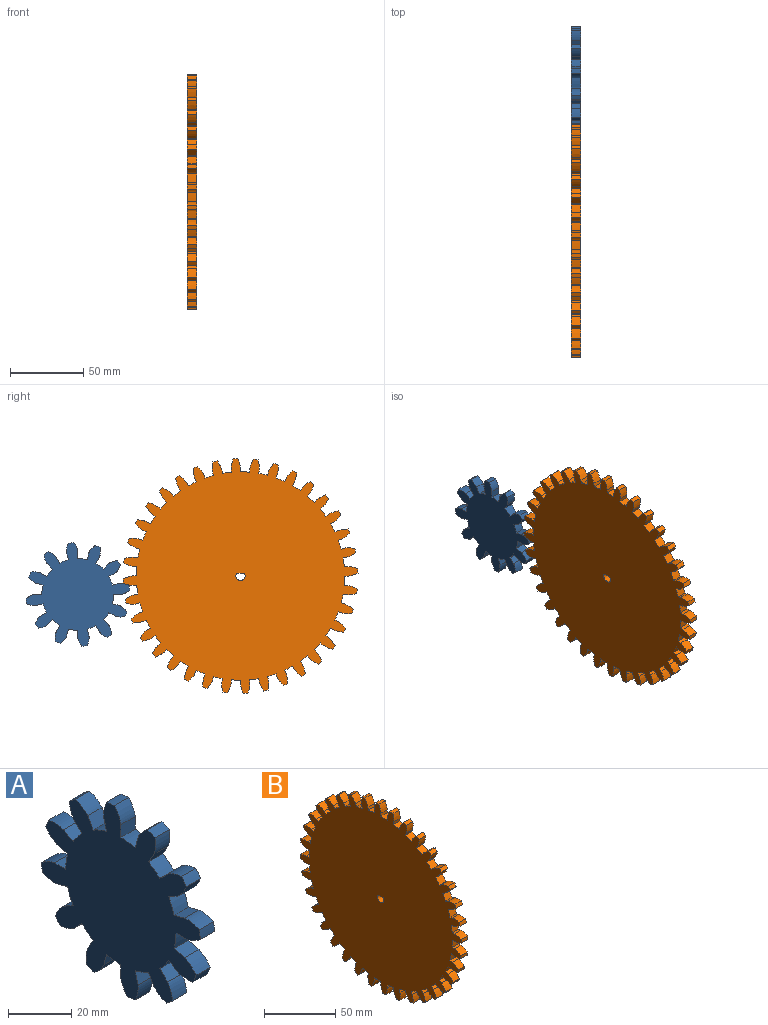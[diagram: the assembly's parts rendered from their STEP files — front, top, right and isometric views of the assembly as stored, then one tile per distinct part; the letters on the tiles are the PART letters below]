
ASSEMBLY  parts=2 mates=1
PART A: 74 faces, bbox 6.4x70.9x70.9 mm
  f0: cylinder r=24.6mm len=6.35mm, axis (-1,0,0), area 40.9mm2, adj f5,f7,f72,f73
  f1: plane 6.35x4.74mm, normal (0,-0.26,0.97), area 31.2mm2, adj f2,f66,f72,f73
  f2: extruded ~6.35x4.99mm, area 42.4mm2, adj f1,f3,f72,f73
  f3: cylinder r=35.56mm len=6.35mm, axis (-1,0,0), area 22.7mm2, adj f2,f4,f72,f73
  f4: extruded ~6.57x6.35mm, area 42.4mm2, adj f3,f5,f72,f73
  f5: plane 6.35x4.25mm, normal (0,0.5,-0.87), area 31.2mm2, adj f0,f4,f72,f73
  f6: cylinder r=24.6mm len=6.35mm, axis (-1,0,0), area 40.9mm2, adj f11,f13,f72,f73
  f7: plane 6.35x3.47mm, normal (0,-0.71,0.71), area 31.2mm2, adj f0,f8,f72,f73
  f8: extruded ~6.35x6.22mm, area 42.4mm2, adj f7,f9,f72,f73
  f9: cylinder r=35.56mm len=6.35mm, axis (-1,0,0), area 22.7mm2, adj f8,f10,f72,f73
  f10: extruded ~6.35x5.45mm, area 42.4mm2, adj f9,f11,f72,f73
  f11: plane 6.35x4.25mm, normal (0,0.87,-0.5), area 31.2mm2, adj f6,f10,f72,f73
  f12: cylinder r=24.6mm len=6.37mm, axis (-1,0,0), area 40.9mm2, adj f17,f19,f72,f73
  f13: plane 6.35x4.74mm, normal (0,-0.97,0.26), area 31.2mm2, adj f6,f14,f72,f73
  f14: extruded ~6.47x6.35mm, area 42.4mm2, adj f13,f15,f72,f73
  f15: cylinder r=35.56mm len=6.35mm, axis (-1,0,0), area 22.7mm2, adj f14,f16,f72,f73
  f16: extruded ~6.35x5.94mm, area 42.4mm2, adj f15,f17,f72,f73
  f17: plane 6.35x4.91mm, normal (0,1,0), area 31.2mm2, adj f12,f16,f72,f73
  f18: cylinder r=24.6mm len=6.35mm, axis (-1,0,0), area 40.9mm2, adj f23,f25,f72,f73
  f19: plane 6.35x4.74mm, normal (0,-0.97,-0.26), area 31.2mm2, adj f12,f20,f72,f73
  f20: extruded ~6.35x4.99mm, area 42.4mm2, adj f19,f21,f72,f73
  f21: cylinder r=35.56mm len=6.35mm, axis (-1,0,0), area 22.7mm2, adj f20,f22,f72,f73
  f22: extruded ~6.57x6.35mm, area 42.4mm2, adj f21,f23,f72,f73
  f23: plane 6.35x4.25mm, normal (0,0.87,0.5), area 31.2mm2, adj f18,f22,f72,f73
  f24: cylinder r=24.6mm len=6.35mm, axis (-1,0,0), area 40.9mm2, adj f29,f31,f72,f73
  f25: plane 6.35x3.47mm, normal (0,-0.71,-0.71), area 31.2mm2, adj f18,f26,f72,f73
  f26: extruded ~6.35x6.22mm, area 42.4mm2, adj f25,f27,f72,f73
  f27: cylinder r=35.56mm len=6.35mm, axis (-1,0,0), area 22.7mm2, adj f26,f28,f72,f73
  f28: extruded ~6.35x5.45mm, area 42.4mm2, adj f27,f29,f72,f73
  f29: plane 6.35x4.25mm, normal (0,0.5,0.87), area 31.2mm2, adj f24,f28,f72,f73
  f30: cylinder r=24.6mm len=6.37mm, axis (-1,0,0), area 40.9mm2, adj f35,f37,f72,f73
  f31: plane 6.35x4.74mm, normal (0,-0.26,-0.97), area 31.2mm2, adj f24,f32,f72,f73
  f32: extruded ~6.47x6.35mm, area 42.4mm2, adj f31,f33,f72,f73
  f33: cylinder r=35.56mm len=6.35mm, axis (-1,0,0), area 22.7mm2, adj f32,f34,f72,f73
  f34: extruded ~6.35x5.94mm, area 42.4mm2, adj f33,f35,f72,f73
  f35: plane 6.35x4.91mm, normal (0,0,1), area 31.2mm2, adj f30,f34,f72,f73
  f36: cylinder r=24.6mm len=6.35mm, axis (-1,0,0), area 40.9mm2, adj f41,f43,f72,f73
  f37: plane 6.35x4.74mm, normal (0,0.26,-0.97), area 31.2mm2, adj f30,f38,f72,f73
  f38: extruded ~6.35x4.99mm, area 42.4mm2, adj f37,f39,f72,f73
  f39: cylinder r=35.56mm len=6.35mm, axis (-1,0,0), area 22.7mm2, adj f38,f40,f72,f73
  f40: extruded ~6.57x6.35mm, area 42.4mm2, adj f39,f41,f72,f73
  f41: plane 6.35x4.25mm, normal (0,-0.5,0.87), area 31.2mm2, adj f36,f40,f72,f73
  f42: cylinder r=24.6mm len=6.35mm, axis (-1,0,0), area 40.9mm2, adj f47,f49,f72,f73
  f43: plane 6.35x3.47mm, normal (0,0.71,-0.71), area 31.2mm2, adj f36,f44,f72,f73
  f44: extruded ~6.35x6.22mm, area 42.4mm2, adj f43,f45,f72,f73
  f45: cylinder r=35.56mm len=6.35mm, axis (-1,0,0), area 22.7mm2, adj f44,f46,f72,f73
  f46: extruded ~6.35x5.45mm, area 42.4mm2, adj f45,f47,f72,f73
  f47: plane 6.35x4.25mm, normal (0,-0.87,0.5), area 31.2mm2, adj f42,f46,f72,f73
  f48: cylinder r=24.6mm len=6.37mm, axis (-1,0,0), area 40.9mm2, adj f53,f55,f72,f73
  f49: plane 6.35x4.74mm, normal (0,0.97,-0.26), area 31.2mm2, adj f42,f50,f72,f73
  f50: extruded ~6.47x6.35mm, area 42.4mm2, adj f49,f51,f72,f73
  f51: cylinder r=35.56mm len=6.35mm, axis (-1,0,0), area 22.7mm2, adj f50,f52,f72,f73
  f52: extruded ~6.35x5.94mm, area 42.4mm2, adj f51,f53,f72,f73
  f53: plane 6.35x4.91mm, normal (0,-1,0), area 31.2mm2, adj f48,f52,f72,f73
  f54: cylinder r=24.6mm len=6.35mm, axis (-1,0,0), area 40.9mm2, adj f59,f61,f72,f73
  f55: plane 6.35x4.74mm, normal (0,0.97,0.26), area 31.2mm2, adj f48,f56,f72,f73
  f56: extruded ~6.35x4.99mm, area 42.4mm2, adj f55,f57,f72,f73
  f57: cylinder r=35.56mm len=6.35mm, axis (-1,0,0), area 22.7mm2, adj f56,f58,f72,f73
  f58: extruded ~6.57x6.35mm, area 42.4mm2, adj f57,f59,f72,f73
  f59: plane 6.35x4.25mm, normal (0,-0.87,-0.5), area 31.2mm2, adj f54,f58,f72,f73
  f60: cylinder r=24.6mm len=6.35mm, axis (-1,0,0), area 40.9mm2, adj f65,f67,f72,f73
  f61: plane 6.35x3.47mm, normal (0,0.71,0.71), area 31.2mm2, adj f54,f62,f72,f73
  f62: extruded ~6.35x6.22mm, area 42.4mm2, adj f61,f63,f72,f73
  f63: cylinder r=35.56mm len=6.35mm, axis (-1,0,0), area 22.7mm2, adj f62,f64,f72,f73
  f64: extruded ~6.35x5.45mm, area 42.4mm2, adj f63,f65,f72,f73
  f65: plane 6.35x4.25mm, normal (0,-0.5,-0.87), area 31.2mm2, adj f60,f64,f72,f73
  f66: cylinder r=24.6mm len=6.37mm, axis (-1,0,0), area 40.9mm2, adj f1,f71,f72,f73
  f67: plane 6.35x4.74mm, normal (0,0.26,0.97), area 31.2mm2, adj f60,f68,f72,f73
  f68: extruded ~6.47x6.35mm, area 42.4mm2, adj f67,f69,f72,f73
  f69: cylinder r=35.56mm len=6.35mm, axis (-1,0,0), area 22.7mm2, adj f68,f70,f72,f73
  f70: extruded ~6.35x5.94mm, area 42.4mm2, adj f69,f71,f72,f73
  f71: plane 6.35x4.91mm, normal (0,0,-1), area 31.2mm2, adj f66,f70,f72,f73
  f72: plane 70.91x70.91mm, normal (1,0,0), area 2775.4mm2, adj f0,f1,f2,f3,f4,f5,f6,f7
  f73: plane 70.91x70.91mm, normal (-1,0,0), area 2775.4mm2, adj f0,f1,f2,f3,f4,f5,f6,f7
PART B: 220 faces, bbox 6.4x160.8x160.8 mm
  f0: cylinder r=71.3mm len=6.35mm, axis (-1,0,0), area 39.5mm2, adj f5,f7,f218,f219
  f1: plane 6.35x2.46mm, normal (0,-0.09,1), area 15.7mm2, adj f2,f210,f218,f219
  f2: extruded ~6.44x6.35mm, area 44.2mm2, adj f1,f3,f218,f219
  f3: cylinder r=80.43mm len=6.35mm, axis (-1,0,0), area 19.4mm2, adj f2,f4,f218,f219
  f4: extruded ~6.88x6.35mm, area 44.2mm2, adj f3,f5,f218,f219
  f5: plane 6.35x2.43mm, normal (0,0.17,-0.98), area 15.7mm2, adj f0,f4,f218,f219
  f6: cylinder r=71.3mm len=6.35mm, axis (-1,0,0), area 39.5mm2, adj f11,f13,f218,f219
  f7: plane 6.35x2.39mm, normal (0,-0.26,0.97), area 15.7mm2, adj f0,f8,f218,f219
  f8: extruded ~6.35x5.9mm, area 44.2mm2, adj f7,f9,f218,f219
  f9: cylinder r=80.43mm len=6.35mm, axis (-1,0,0), area 19.4mm2, adj f8,f10,f218,f219
  f10: extruded ~6.91x6.35mm, area 44.2mm2, adj f9,f11,f218,f219
  f11: plane 6.35x2.32mm, normal (0,0.34,-0.94), area 15.7mm2, adj f6,f10,f218,f219
  f12: cylinder r=71.3mm len=6.35mm, axis (-1,0,0), area 39.5mm2, adj f17,f19,f218,f219
  f13: plane 6.35x2.24mm, normal (0,-0.42,0.91), area 15.7mm2, adj f6,f14,f218,f219
  f14: extruded ~6.35x5.18mm, area 44.2mm2, adj f13,f15,f218,f219
  f15: cylinder r=80.43mm len=6.35mm, axis (-1,0,0), area 19.4mm2, adj f14,f16,f218,f219
  f16: extruded ~6.74x6.35mm, area 44.2mm2, adj f15,f17,f218,f219
  f17: plane 6.35x2.14mm, normal (0,0.5,-0.87), area 15.7mm2, adj f12,f16,f218,f219
  f18: cylinder r=71.3mm len=6.35mm, axis (-1,0,0), area 39.5mm2, adj f23,f25,f218,f219
  f19: plane 6.35x2.02mm, normal (0,-0.57,0.82), area 15.7mm2, adj f12,f20,f218,f219
  f20: extruded ~6.35x5.43mm, area 44.2mm2, adj f19,f21,f218,f219
  f21: cylinder r=80.43mm len=6.35mm, axis (-1,0,0), area 19.4mm2, adj f20,f22,f218,f219
  f22: extruded ~6.36x6.35mm, area 44.2mm2, adj f21,f23,f218,f219
  f23: plane 6.35x1.89mm, normal (0,0.64,-0.77), area 15.7mm2, adj f18,f22,f218,f219
  f24: cylinder r=71.3mm len=6.35mm, axis (-1,0,0), area 39.5mm2, adj f29,f31,f218,f219
  f25: plane 6.35x1.75mm, normal (0,-0.71,0.71), area 15.7mm2, adj f18,f26,f218,f219
  f26: extruded ~6.35x6.09mm, area 44.2mm2, adj f25,f27,f218,f219
  f27: cylinder r=80.43mm len=6.35mm, axis (-1,0,0), area 19.4mm2, adj f26,f28,f218,f219
  f28: extruded ~6.35x5.78mm, area 44.2mm2, adj f27,f29,f218,f219
  f29: plane 6.35x1.89mm, normal (0,0.77,-0.64), area 15.7mm2, adj f24,f28,f218,f219
  f30: cylinder r=71.3mm len=6.35mm, axis (-1,0,0), area 39.5mm2, adj f35,f37,f218,f219
  f31: plane 6.35x2.02mm, normal (0,-0.82,0.57), area 15.7mm2, adj f24,f32,f218,f219
  f32: extruded ~6.57x6.35mm, area 44.2mm2, adj f31,f33,f218,f219
  f33: cylinder r=80.43mm len=6.35mm, axis (-1,0,0), area 19.4mm2, adj f32,f34,f218,f219
  f34: extruded ~6.35x5.03mm, area 44.2mm2, adj f33,f35,f218,f219
  f35: plane 6.35x2.14mm, normal (0,0.87,-0.5), area 15.7mm2, adj f30,f34,f218,f219
  f36: cylinder r=71.3mm len=6.35mm, axis (-1,0,0), area 39.5mm2, adj f41,f43,f218,f219
  f37: plane 6.35x2.24mm, normal (0,-0.91,0.42), area 15.7mm2, adj f30,f38,f218,f219
  f38: extruded ~6.85x6.35mm, area 44.2mm2, adj f37,f39,f218,f219
  f39: cylinder r=80.43mm len=6.35mm, axis (-1,0,0), area 19.4mm2, adj f38,f40,f218,f219
  f40: extruded ~6.35x5.56mm, area 44.2mm2, adj f39,f41,f218,f219
  f41: plane 6.35x2.32mm, normal (0,0.94,-0.34), area 15.7mm2, adj f36,f40,f218,f219
  f42: cylinder r=71.3mm len=6.35mm, axis (-1,0,0), area 39.5mm2, adj f47,f49,f218,f219
  f43: plane 6.35x2.39mm, normal (0,-0.97,0.26), area 15.7mm2, adj f36,f44,f218,f219
  f44: extruded ~6.92x6.35mm, area 44.2mm2, adj f43,f45,f218,f219
  f45: cylinder r=80.43mm len=6.35mm, axis (-1,0,0), area 19.4mm2, adj f44,f46,f218,f219
  f46: extruded ~6.35x6.19mm, area 44.2mm2, adj f45,f47,f218,f219
  f47: plane 6.35x2.43mm, normal (0,0.98,-0.17), area 15.7mm2, adj f42,f46,f218,f219
  f48: cylinder r=71.3mm len=6.35mm, axis (-1,0,0), area 39.5mm2, adj f53,f55,f218,f219
  f49: plane 6.35x2.46mm, normal (0,-1,0.09), area 15.7mm2, adj f42,f50,f218,f219
  f50: extruded ~6.78x6.35mm, area 44.2mm2, adj f49,f51,f218,f219
  f51: cylinder r=80.43mm len=6.35mm, axis (-1,0,0), area 19.4mm2, adj f50,f52,f218,f219
  f52: extruded ~6.64x6.35mm, area 44.2mm2, adj f51,f53,f218,f219
  f53: plane 6.35x2.47mm, normal (0,1,0), area 15.7mm2, adj f48,f52,f218,f219
  f54: cylinder r=71.3mm len=6.35mm, axis (-1,0,0), area 39.5mm2, adj f59,f61,f218,f219
  f55: plane 6.35x2.46mm, normal (0,-1,-0.09), area 15.7mm2, adj f48,f56,f218,f219
  f56: extruded ~6.44x6.35mm, area 44.2mm2, adj f55,f57,f218,f219
  f57: cylinder r=80.43mm len=6.35mm, axis (-1,0,0), area 19.4mm2, adj f56,f58,f218,f219
  f58: extruded ~6.88x6.35mm, area 44.2mm2, adj f57,f59,f218,f219
  f59: plane 6.35x2.43mm, normal (0,0.98,0.17), area 15.7mm2, adj f54,f58,f218,f219
  f60: cylinder r=71.3mm len=6.35mm, axis (-1,0,0), area 39.5mm2, adj f65,f67,f218,f219
  f61: plane 6.35x2.39mm, normal (0,-0.97,-0.26), area 15.7mm2, adj f54,f62,f218,f219
  f62: extruded ~6.35x5.9mm, area 44.2mm2, adj f61,f63,f218,f219
  f63: cylinder r=80.43mm len=6.35mm, axis (-1,0,0), area 19.4mm2, adj f62,f64,f218,f219
  f64: extruded ~6.91x6.35mm, area 44.2mm2, adj f63,f65,f218,f219
  f65: plane 6.35x2.32mm, normal (0,0.94,0.34), area 15.7mm2, adj f60,f64,f218,f219
  f66: cylinder r=71.3mm len=6.35mm, axis (-1,0,0), area 39.5mm2, adj f71,f73,f218,f219
  f67: plane 6.35x2.24mm, normal (0,-0.91,-0.42), area 15.7mm2, adj f60,f68,f218,f219
  f68: extruded ~6.35x5.18mm, area 44.2mm2, adj f67,f69,f218,f219
  f69: cylinder r=80.43mm len=6.35mm, axis (-1,0,0), area 19.4mm2, adj f68,f70,f218,f219
  f70: extruded ~6.74x6.35mm, area 44.2mm2, adj f69,f71,f218,f219
  f71: plane 6.35x2.14mm, normal (0,0.87,0.5), area 15.7mm2, adj f66,f70,f218,f219
  f72: cylinder r=71.3mm len=6.35mm, axis (-1,0,0), area 39.5mm2, adj f77,f79,f218,f219
  f73: plane 6.35x2.02mm, normal (0,-0.82,-0.57), area 15.7mm2, adj f66,f74,f218,f219
  f74: extruded ~6.35x5.43mm, area 44.2mm2, adj f73,f75,f218,f219
  f75: cylinder r=80.43mm len=6.35mm, axis (-1,0,0), area 19.4mm2, adj f74,f76,f218,f219
  f76: extruded ~6.36x6.35mm, area 44.2mm2, adj f75,f77,f218,f219
  f77: plane 6.35x1.89mm, normal (0,0.77,0.64), area 15.7mm2, adj f72,f76,f218,f219
  f78: cylinder r=71.3mm len=6.35mm, axis (-1,0,0), area 39.5mm2, adj f83,f85,f218,f219
  f79: plane 6.35x1.75mm, normal (0,-0.71,-0.71), area 15.7mm2, adj f72,f80,f218,f219
  f80: extruded ~6.35x6.09mm, area 44.2mm2, adj f79,f81,f218,f219
  f81: cylinder r=80.43mm len=6.35mm, axis (-1,0,0), area 19.4mm2, adj f80,f82,f218,f219
  f82: extruded ~6.35x5.78mm, area 44.2mm2, adj f81,f83,f218,f219
  f83: plane 6.35x1.89mm, normal (0,0.64,0.77), area 15.7mm2, adj f78,f82,f218,f219
  f84: cylinder r=71.3mm len=6.35mm, axis (-1,0,0), area 39.5mm2, adj f89,f91,f218,f219
  f85: plane 6.35x2.02mm, normal (0,-0.57,-0.82), area 15.7mm2, adj f78,f86,f218,f219
  f86: extruded ~6.57x6.35mm, area 44.2mm2, adj f85,f87,f218,f219
  f87: cylinder r=80.43mm len=6.35mm, axis (-1,0,0), area 19.4mm2, adj f86,f88,f218,f219
  f88: extruded ~6.35x5.03mm, area 44.2mm2, adj f87,f89,f218,f219
  f89: plane 6.35x2.14mm, normal (0,0.5,0.87), area 15.7mm2, adj f84,f88,f218,f219
  f90: cylinder r=71.3mm len=6.35mm, axis (-1,0,0), area 39.5mm2, adj f95,f97,f218,f219
  f91: plane 6.35x2.24mm, normal (0,-0.42,-0.91), area 15.7mm2, adj f84,f92,f218,f219
  f92: extruded ~6.85x6.35mm, area 44.2mm2, adj f91,f93,f218,f219
  f93: cylinder r=80.43mm len=6.35mm, axis (-1,0,0), area 19.4mm2, adj f92,f94,f218,f219
  f94: extruded ~6.35x5.56mm, area 44.2mm2, adj f93,f95,f218,f219
  f95: plane 6.35x2.32mm, normal (0,0.34,0.94), area 15.7mm2, adj f90,f94,f218,f219
  f96: cylinder r=71.3mm len=6.35mm, axis (-1,0,0), area 39.5mm2, adj f101,f103,f218,f219
  f97: plane 6.35x2.39mm, normal (0,-0.26,-0.97), area 15.7mm2, adj f90,f98,f218,f219
  f98: extruded ~6.92x6.35mm, area 44.2mm2, adj f97,f99,f218,f219
  f99: cylinder r=80.43mm len=6.35mm, axis (-1,0,0), area 19.4mm2, adj f98,f100,f218,f219
  f100: extruded ~6.35x6.19mm, area 44.2mm2, adj f99,f101,f218,f219
  f101: plane 6.35x2.43mm, normal (0,0.17,0.98), area 15.7mm2, adj f96,f100,f218,f219
  f102: cylinder r=71.3mm len=6.35mm, axis (-1,0,0), area 39.5mm2, adj f107,f109,f218,f219
  f103: plane 6.35x2.46mm, normal (0,-0.09,-1), area 15.7mm2, adj f96,f104,f218,f219
  f104: extruded ~6.78x6.35mm, area 44.2mm2, adj f103,f105,f218,f219
  f105: cylinder r=80.43mm len=6.35mm, axis (-1,0,0), area 19.4mm2, adj f104,f106,f218,f219
  f106: extruded ~6.64x6.35mm, area 44.2mm2, adj f105,f107,f218,f219
  f107: plane 6.35x2.47mm, normal (0,0,1), area 15.7mm2, adj f102,f106,f218,f219
  f108: cylinder r=71.3mm len=6.35mm, axis (-1,0,0), area 39.5mm2, adj f113,f115,f218,f219
  f109: plane 6.35x2.46mm, normal (0,0.09,-1), area 15.7mm2, adj f102,f110,f218,f219
  f110: extruded ~6.44x6.35mm, area 44.2mm2, adj f109,f111,f218,f219
  f111: cylinder r=80.43mm len=6.35mm, axis (-1,0,0), area 19.4mm2, adj f110,f112,f218,f219
  f112: extruded ~6.88x6.35mm, area 44.2mm2, adj f111,f113,f218,f219
  f113: plane 6.35x2.43mm, normal (0,-0.17,0.98), area 15.7mm2, adj f108,f112,f218,f219
  f114: cylinder r=71.3mm len=6.35mm, axis (-1,0,0), area 39.5mm2, adj f119,f121,f218,f219
  f115: plane 6.35x2.39mm, normal (0,0.26,-0.97), area 15.7mm2, adj f108,f116,f218,f219
  f116: extruded ~6.35x5.9mm, area 44.2mm2, adj f115,f117,f218,f219
  f117: cylinder r=80.43mm len=6.35mm, axis (-1,0,0), area 19.4mm2, adj f116,f118,f218,f219
  f118: extruded ~6.91x6.35mm, area 44.2mm2, adj f117,f119,f218,f219
  f119: plane 6.35x2.32mm, normal (0,-0.34,0.94), area 15.7mm2, adj f114,f118,f218,f219
  f120: cylinder r=71.3mm len=6.35mm, axis (-1,0,0), area 39.5mm2, adj f125,f127,f218,f219
  f121: plane 6.35x2.24mm, normal (0,0.42,-0.91), area 15.7mm2, adj f114,f122,f218,f219
  f122: extruded ~6.35x5.18mm, area 44.2mm2, adj f121,f123,f218,f219
  f123: cylinder r=80.43mm len=6.35mm, axis (-1,0,0), area 19.4mm2, adj f122,f124,f218,f219
  f124: extruded ~6.74x6.35mm, area 44.2mm2, adj f123,f125,f218,f219
  f125: plane 6.35x2.14mm, normal (0,-0.5,0.87), area 15.7mm2, adj f120,f124,f218,f219
  f126: cylinder r=71.3mm len=6.35mm, axis (-1,0,0), area 39.5mm2, adj f131,f133,f218,f219
  f127: plane 6.35x2.02mm, normal (0,0.57,-0.82), area 15.7mm2, adj f120,f128,f218,f219
  f128: extruded ~6.35x5.43mm, area 44.2mm2, adj f127,f129,f218,f219
  f129: cylinder r=80.43mm len=6.35mm, axis (-1,0,0), area 19.4mm2, adj f128,f130,f218,f219
  f130: extruded ~6.36x6.35mm, area 44.2mm2, adj f129,f131,f218,f219
  f131: plane 6.35x1.89mm, normal (0,-0.64,0.77), area 15.7mm2, adj f126,f130,f218,f219
  f132: cylinder r=71.3mm len=6.35mm, axis (-1,0,0), area 39.5mm2, adj f137,f139,f218,f219
  f133: plane 6.35x1.75mm, normal (0,0.71,-0.71), area 15.7mm2, adj f126,f134,f218,f219
  f134: extruded ~6.35x6.09mm, area 44.2mm2, adj f133,f135,f218,f219
  f135: cylinder r=80.43mm len=6.35mm, axis (-1,0,0), area 19.4mm2, adj f134,f136,f218,f219
  f136: extruded ~6.35x5.78mm, area 44.2mm2, adj f135,f137,f218,f219
  f137: plane 6.35x1.89mm, normal (0,-0.77,0.64), area 15.7mm2, adj f132,f136,f218,f219
  f138: cylinder r=71.3mm len=6.35mm, axis (-1,0,0), area 39.5mm2, adj f143,f145,f218,f219
  f139: plane 6.35x2.02mm, normal (0,0.82,-0.57), area 15.7mm2, adj f132,f140,f218,f219
  f140: extruded ~6.57x6.35mm, area 44.2mm2, adj f139,f141,f218,f219
  f141: cylinder r=80.43mm len=6.35mm, axis (-1,0,0), area 19.4mm2, adj f140,f142,f218,f219
  f142: extruded ~6.35x5.03mm, area 44.2mm2, adj f141,f143,f218,f219
  f143: plane 6.35x2.14mm, normal (0,-0.87,0.5), area 15.7mm2, adj f138,f142,f218,f219
  f144: cylinder r=71.3mm len=6.35mm, axis (-1,0,0), area 39.5mm2, adj f149,f151,f218,f219
  f145: plane 6.35x2.24mm, normal (0,0.91,-0.42), area 15.7mm2, adj f138,f146,f218,f219
  f146: extruded ~6.85x6.35mm, area 44.2mm2, adj f145,f147,f218,f219
  f147: cylinder r=80.43mm len=6.35mm, axis (-1,0,0), area 19.4mm2, adj f146,f148,f218,f219
  f148: extruded ~6.35x5.56mm, area 44.2mm2, adj f147,f149,f218,f219
  f149: plane 6.35x2.32mm, normal (0,-0.94,0.34), area 15.7mm2, adj f144,f148,f218,f219
  f150: cylinder r=71.3mm len=6.35mm, axis (-1,0,0), area 39.5mm2, adj f155,f157,f218,f219
  f151: plane 6.35x2.39mm, normal (0,0.97,-0.26), area 15.7mm2, adj f144,f152,f218,f219
  f152: extruded ~6.92x6.35mm, area 44.2mm2, adj f151,f153,f218,f219
  f153: cylinder r=80.43mm len=6.35mm, axis (-1,0,0), area 19.4mm2, adj f152,f154,f218,f219
  f154: extruded ~6.35x6.19mm, area 44.2mm2, adj f153,f155,f218,f219
  f155: plane 6.35x2.43mm, normal (0,-0.98,0.17), area 15.7mm2, adj f150,f154,f218,f219
  f156: cylinder r=71.3mm len=6.35mm, axis (-1,0,0), area 39.5mm2, adj f161,f163,f218,f219
  f157: plane 6.35x2.46mm, normal (0,1,-0.09), area 15.7mm2, adj f150,f158,f218,f219
  f158: extruded ~6.78x6.35mm, area 44.2mm2, adj f157,f159,f218,f219
  f159: cylinder r=80.43mm len=6.35mm, axis (-1,0,0), area 19.4mm2, adj f158,f160,f218,f219
  f160: extruded ~6.64x6.35mm, area 44.2mm2, adj f159,f161,f218,f219
  f161: plane 6.35x2.47mm, normal (0,-1,0), area 15.7mm2, adj f156,f160,f218,f219
  f162: cylinder r=71.3mm len=6.35mm, axis (-1,0,0), area 39.5mm2, adj f167,f169,f218,f219
  f163: plane 6.35x2.46mm, normal (0,1,0.09), area 15.7mm2, adj f156,f164,f218,f219
  f164: extruded ~6.44x6.35mm, area 44.2mm2, adj f163,f165,f218,f219
  f165: cylinder r=80.43mm len=6.35mm, axis (-1,0,0), area 19.4mm2, adj f164,f166,f218,f219
  f166: extruded ~6.88x6.35mm, area 44.2mm2, adj f165,f167,f218,f219
  f167: plane 6.35x2.43mm, normal (0,-0.98,-0.17), area 15.7mm2, adj f162,f166,f218,f219
  f168: cylinder r=71.3mm len=6.35mm, axis (-1,0,0), area 39.5mm2, adj f173,f175,f218,f219
  f169: plane 6.35x2.39mm, normal (0,0.97,0.26), area 15.7mm2, adj f162,f170,f218,f219
  f170: extruded ~6.35x5.9mm, area 44.2mm2, adj f169,f171,f218,f219
  f171: cylinder r=80.43mm len=6.35mm, axis (-1,0,0), area 19.4mm2, adj f170,f172,f218,f219
  f172: extruded ~6.91x6.35mm, area 44.2mm2, adj f171,f173,f218,f219
  f173: plane 6.35x2.32mm, normal (0,-0.94,-0.34), area 15.7mm2, adj f168,f172,f218,f219
  f174: cylinder r=71.3mm len=6.35mm, axis (-1,0,0), area 39.5mm2, adj f179,f181,f218,f219
  f175: plane 6.35x2.24mm, normal (0,0.91,0.42), area 15.7mm2, adj f168,f176,f218,f219
  f176: extruded ~6.35x5.18mm, area 44.2mm2, adj f175,f177,f218,f219
  f177: cylinder r=80.43mm len=6.35mm, axis (-1,0,0), area 19.4mm2, adj f176,f178,f218,f219
  f178: extruded ~6.74x6.35mm, area 44.2mm2, adj f177,f179,f218,f219
  f179: plane 6.35x2.14mm, normal (0,-0.87,-0.5), area 15.7mm2, adj f174,f178,f218,f219
  f180: cylinder r=71.3mm len=6.35mm, axis (-1,0,0), area 39.5mm2, adj f185,f187,f218,f219
  f181: plane 6.35x2.02mm, normal (0,0.82,0.57), area 15.7mm2, adj f174,f182,f218,f219
  f182: extruded ~6.35x5.43mm, area 44.2mm2, adj f181,f183,f218,f219
  f183: cylinder r=80.43mm len=6.35mm, axis (-1,0,0), area 19.4mm2, adj f182,f184,f218,f219
  f184: extruded ~6.36x6.35mm, area 44.2mm2, adj f183,f185,f218,f219
  f185: plane 6.35x1.89mm, normal (0,-0.77,-0.64), area 15.7mm2, adj f180,f184,f218,f219
  f186: cylinder r=71.3mm len=6.35mm, axis (-1,0,0), area 39.5mm2, adj f191,f193,f218,f219
  f187: plane 6.35x1.75mm, normal (0,0.71,0.71), area 15.7mm2, adj f180,f188,f218,f219
  f188: extruded ~6.35x6.09mm, area 44.2mm2, adj f187,f189,f218,f219
  f189: cylinder r=80.43mm len=6.35mm, axis (-1,0,0), area 19.4mm2, adj f188,f190,f218,f219
  f190: extruded ~6.35x5.78mm, area 44.2mm2, adj f189,f191,f218,f219
  f191: plane 6.35x1.89mm, normal (0,-0.64,-0.77), area 15.7mm2, adj f186,f190,f218,f219
  f192: cylinder r=71.3mm len=6.35mm, axis (-1,0,0), area 39.5mm2, adj f197,f199,f218,f219
  f193: plane 6.35x2.02mm, normal (0,0.57,0.82), area 15.7mm2, adj f186,f194,f218,f219
  f194: extruded ~6.57x6.35mm, area 44.2mm2, adj f193,f195,f218,f219
  f195: cylinder r=80.43mm len=6.35mm, axis (-1,0,0), area 19.4mm2, adj f194,f196,f218,f219
  f196: extruded ~6.35x5.03mm, area 44.2mm2, adj f195,f197,f218,f219
  f197: plane 6.35x2.14mm, normal (0,-0.5,-0.87), area 15.7mm2, adj f192,f196,f218,f219
  f198: cylinder r=71.3mm len=6.35mm, axis (-1,0,0), area 39.5mm2, adj f203,f205,f218,f219
  f199: plane 6.35x2.24mm, normal (0,0.42,0.91), area 15.7mm2, adj f192,f200,f218,f219
  f200: extruded ~6.85x6.35mm, area 44.2mm2, adj f199,f201,f218,f219
  f201: cylinder r=80.43mm len=6.35mm, axis (-1,0,0), area 19.4mm2, adj f200,f202,f218,f219
  f202: extruded ~6.35x5.56mm, area 44.2mm2, adj f201,f203,f218,f219
  f203: plane 6.35x2.32mm, normal (0,-0.34,-0.94), area 15.7mm2, adj f198,f202,f218,f219
  f204: cylinder r=71.3mm len=6.35mm, axis (-1,0,0), area 39.5mm2, adj f209,f211,f218,f219
  f205: plane 6.35x2.39mm, normal (0,0.26,0.97), area 15.7mm2, adj f198,f206,f218,f219
  f206: extruded ~6.92x6.35mm, area 44.2mm2, adj f205,f207,f218,f219
  f207: cylinder r=80.43mm len=6.35mm, axis (-1,0,0), area 19.4mm2, adj f206,f208,f218,f219
  f208: extruded ~6.35x6.19mm, area 44.2mm2, adj f207,f209,f218,f219
  f209: plane 6.35x2.43mm, normal (0,-0.17,-0.98), area 15.7mm2, adj f204,f208,f218,f219
  f210: cylinder r=71.3mm len=6.35mm, axis (-1,0,0), area 39.5mm2, adj f1,f217,f218,f219
  f211: plane 6.35x2.46mm, normal (0,0.09,1), area 15.7mm2, adj f204,f212,f218,f219
  f212: extruded ~6.78x6.35mm, area 44.2mm2, adj f211,f213,f218,f219
  f213: cylinder r=80.43mm len=6.35mm, axis (-1,0,0), area 19.4mm2, adj f212,f214,f218,f219
  f214: extruded ~6.64x6.35mm, area 44.2mm2, adj f213,f217,f218,f219
  f215: cylinder r=3.18mm len=6.35mm, axis (-1,0,0), area 91.6mm2, adj f216,f218,f219
  f216: plane 6.35x4.86mm, normal (0,0,-1), area 30.8mm2, adj f215,f218,f219
  f217: plane 6.35x2.47mm, normal (0,0,-1), area 15.7mm2, adj f210,f214,f218,f219
  f218: plane 160.83x160.83mm, normal (1,0,0), area 17745.8mm2, adj f0,f1,f2,f3,f4,f5,f6,f7
  f219: plane 160.83x160.83mm, normal (-1,0,0), area 17745.8mm2, adj f0,f1,f2,f3,f4,f5,f6,f7
PLACE A t=(-11.43,-2.69,-5.97)mm
PLACE B t=(-11.43,-114.06,6.66)mm
MATE revolute B.f218 <-> A.f72  axis (1,0,0) through (-5.08,-33.78,1.62)mm
